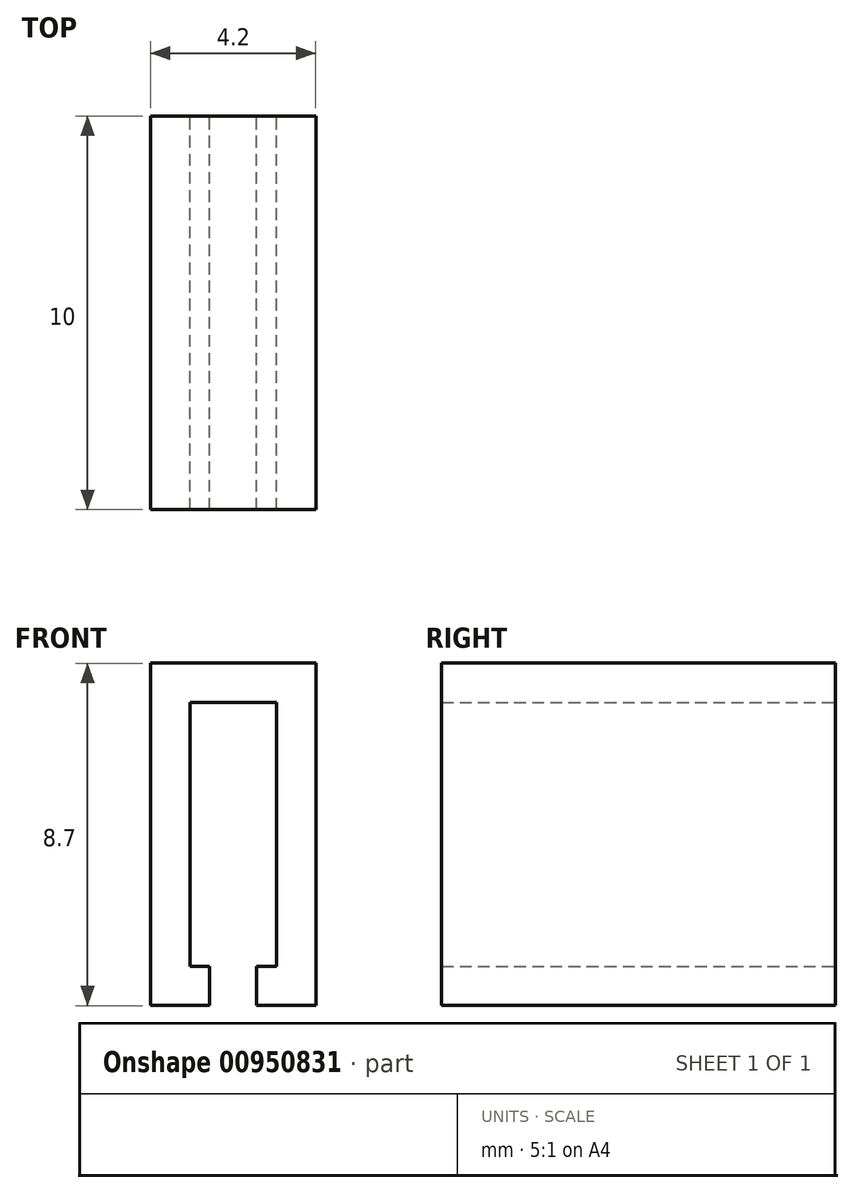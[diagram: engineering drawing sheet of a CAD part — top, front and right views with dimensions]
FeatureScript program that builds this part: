
annotation { "Feature Type Name" : "Feature", "Feature Type Description" : "" }
export const myFeature = defineFeature(function(context is Context, id is Id, definition is map)
    precondition{}
    {
        {
            var Q0;
            Q0=qCreatedBy(makeId("Front.planeOp"),FACE);
            var sketch = newSketch(context, id + "F0", { "sketchPlane" : qUnion([Q0])});
            skLineSegment(sketch, "E0", {"start": v(7.26, -14.57) * mm, "end": v(8.76, -14.57) * mm});
            skLineSegment(sketch, "E1", {"start": v(8.76, -14.57) * mm, "end": v(8.76, -5.87) * mm});
            skLineSegment(sketch, "E2", {"start": v(8.76, -5.87) * mm, "end": v(4.56, -5.87) * mm});
            skLineSegment(sketch, "E3", {"start": v(4.56, -5.87) * mm, "end": v(4.56, -14.57) * mm});
            skLineSegment(sketch, "E4", {"start": v(4.56, -14.57) * mm, "end": v(6.06, -14.57) * mm});
            skLineSegment(sketch, "E5", {"start": v(6.06, -14.57) * mm, "end": v(6.06, -13.57) * mm});
            skLineSegment(sketch, "E6", {"start": v(6.06, -13.57) * mm, "end": v(5.56, -13.57) * mm});
            skLineSegment(sketch, "E7", {"start": v(5.56, -13.57) * mm, "end": v(5.56, -6.87) * mm});
            skLineSegment(sketch, "E8", {"start": v(7.76, -6.87) * mm, "end": v(7.76, -13.57) * mm});
            skLineSegment(sketch, "E9", {"start": v(7.76, -13.57) * mm, "end": v(7.26, -13.57) * mm});
            skLineSegment(sketch, "E10", {"start": v(7.26, -13.57) * mm, "end": v(7.26, -14.57) * mm});
            skLineSegment(sketch, "E11", {"start": v(5.56, -6.87) * mm, "end": v(7.76, -6.87) * mm});
            skSolve(sketch);
        }
        {
            var Q0;
            Q0 = qSketchRegion(id + "F0", true);
            extrude(context, id + "F1", {"entities" : qUnion([Q0]), "depth" : 10 * mm, "offsetDistance" : 25 * mm});
        }
    });
